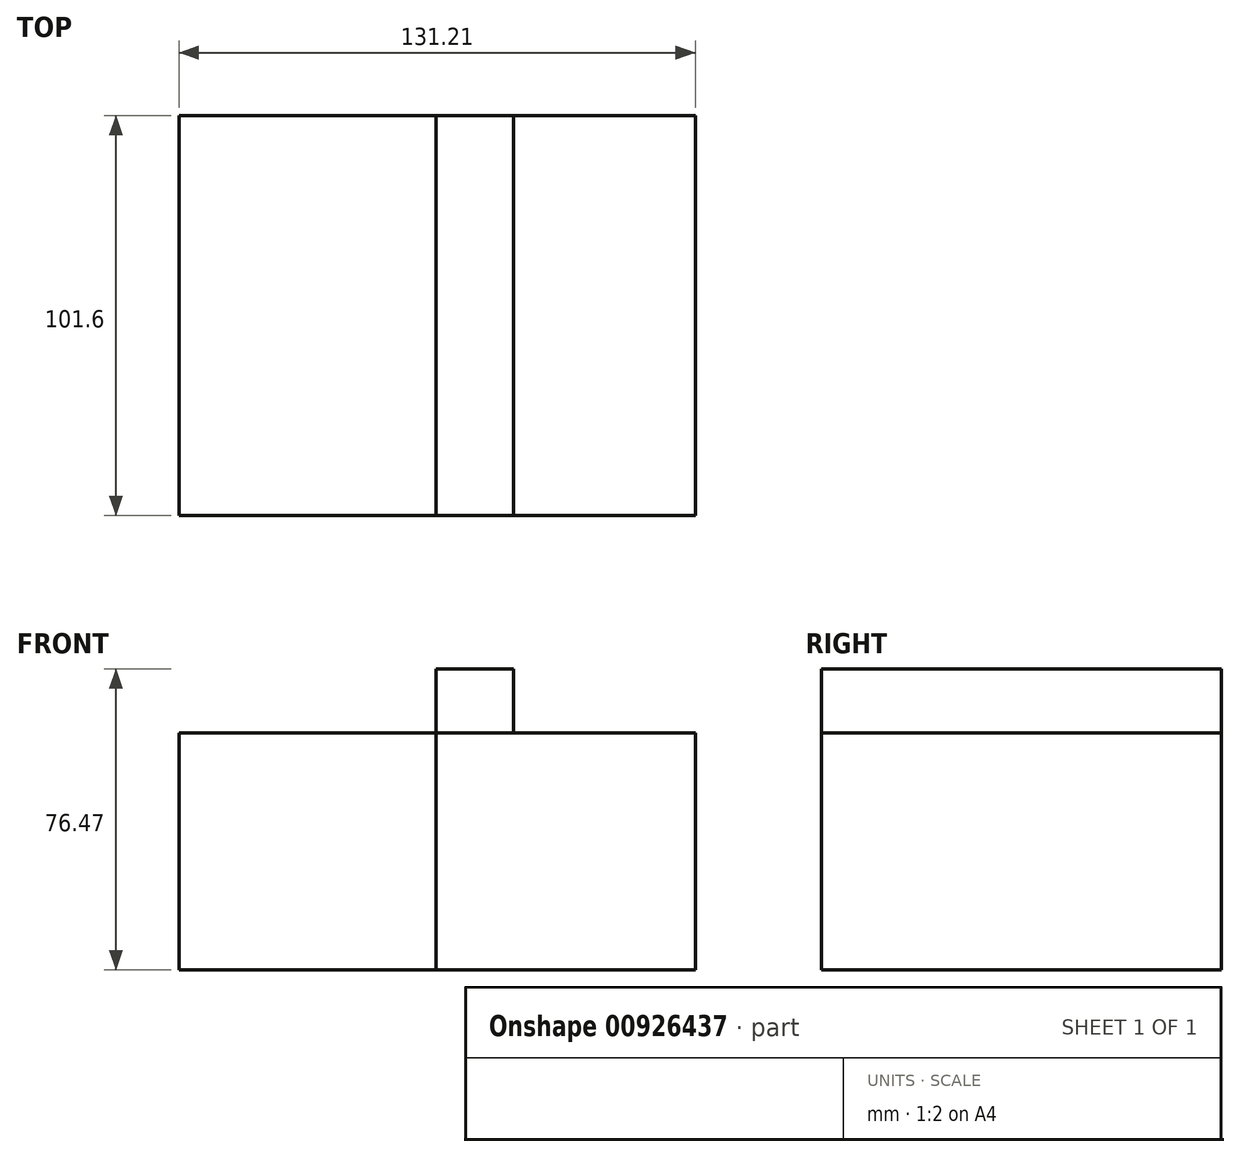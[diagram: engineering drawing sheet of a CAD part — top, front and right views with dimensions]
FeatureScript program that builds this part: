
annotation { "Feature Type Name" : "Feature", "Feature Type Description" : "" }
export const myFeature = defineFeature(function(context is Context, id is Id, definition is map)
    precondition{}
    {
        {
            var Q0;
            Q0=qCreatedBy(makeId("Front.planeOp"),FACE);
            var sketch = newSketch(context, id + "F0", { "sketchPlane" : qUnion([Q0])});
            skLineSegment(sketch, "E0.bottom", {"start": v(65.33, 60.23) * mm, "end": v(0, 60.23) * mm});
            skLineSegment(sketch, "E0.top", {"start": v(65.33, 0) * mm, "end": v(0, 0) * mm});
            skLineSegment(sketch, "E0.left", {"start": v(65.33, 60.23) * mm, "end": v(65.33, 0) * mm});
            skLineSegment(sketch, "E0.right", {"start": v(0, 60.23) * mm, "end": v(0, 0) * mm});
            skLineSegment(sketch, "E1.bottom", {"start": v(84.96, 76.47) * mm, "end": v(65.33, 76.47) * mm});
            skLineSegment(sketch, "E1.top", {"start": v(84.96, 60.23) * mm, "end": v(65.33, 60.23) * mm});
            skLineSegment(sketch, "E1.left", {"start": v(84.96, 76.47) * mm, "end": v(84.96, 60.23) * mm});
            skLineSegment(sketch, "E1.right", {"start": v(65.33, 76.47) * mm, "end": v(65.33, 60.23) * mm});
            skSolve(sketch);
        }
        {
            var Q0;
            Q0 = qSketchRegion(id + "F0", true);
            extrude(context, id + "F1", {"entities" : qUnion([Q0]), "depth" : 101.6 * mm, "offsetDistance" : 25.4 * mm});
        }
        {
            var Q0;
            Q0=makeQuery(id+"F1.opExtrude","SWEPT_FACE",FACE,{"disambiguationData":[OSD([sQuery(id+"F0.wireOp",EDGE,"E0.right")])]});
            var sketch = newSketch(context, id + "F2", { "sketchPlane" : qUnion([Q0])});
            skSolve(sketch);
        }
        {
            var Q0;
            {var subQ0=sQuery(id+"F0.wireOp",EDGE,"E0.right");Q0=makeQuery(id+"F2.imprint","IMPRINT",FACE,{"disambiguationData":[TD([[makeQuery(id+"F2.imprint","IMPRINT",EDGE,{"derivedFrom":makeQuery(id+"F1.opExtrude","CAP_EDGE",EDGE,{"disambiguationData":[OSD([subQ0])],"isStart":true})}),1.0]])]});}
            extrude(context, id + "F3", {"entities" : qUnion([Q0]), "oppositeDirection" : true, "depth" : 131.21 * mm, "offsetDistance" : 25.4 * mm});
        }
    });
